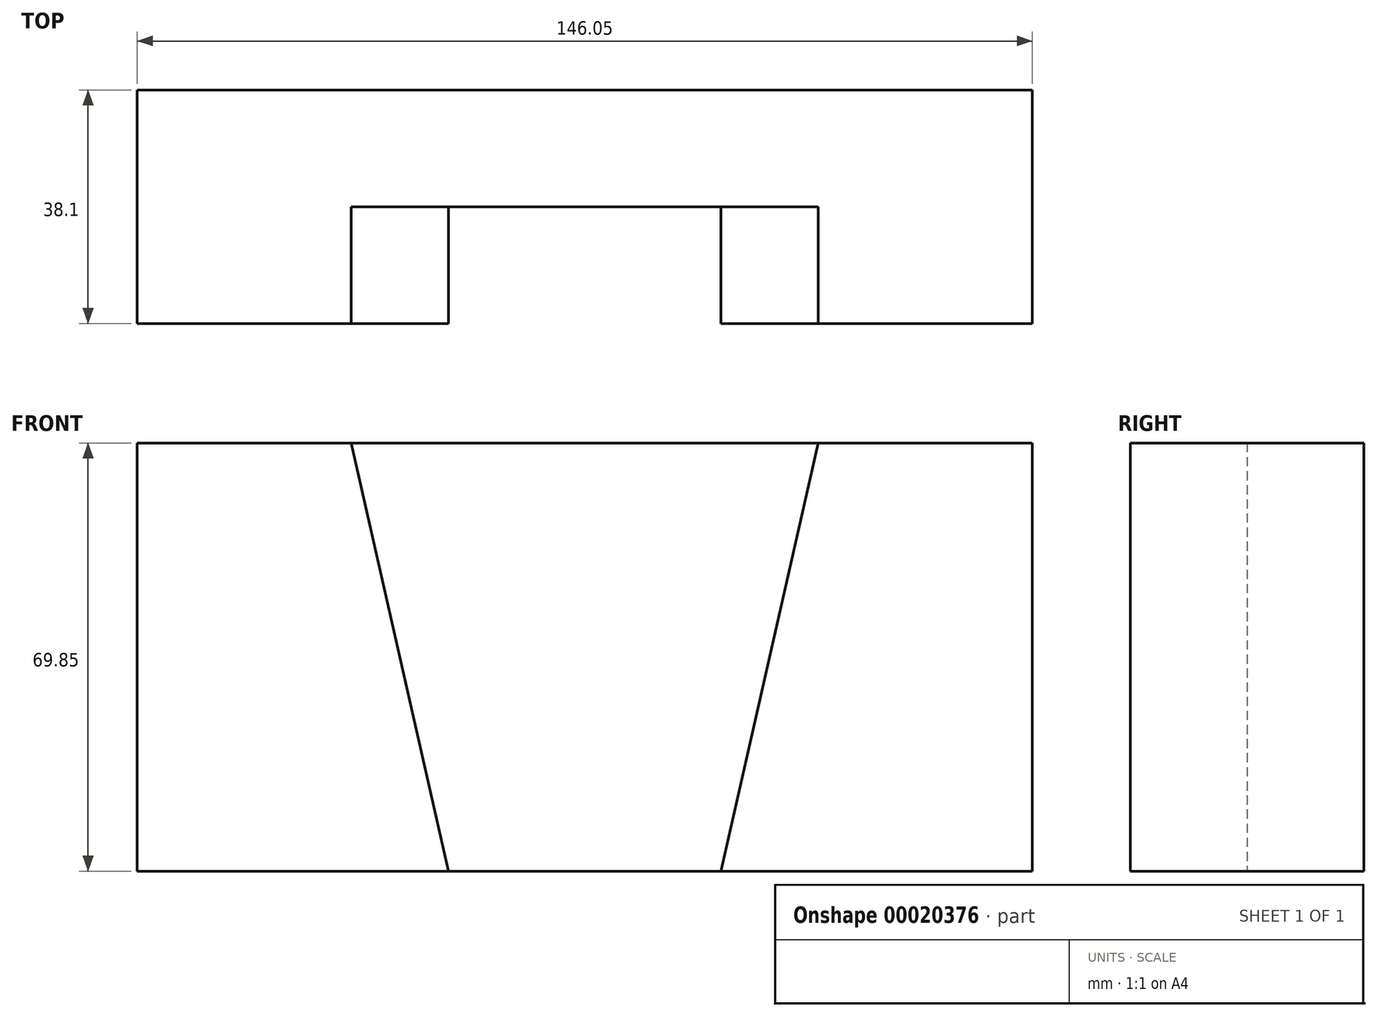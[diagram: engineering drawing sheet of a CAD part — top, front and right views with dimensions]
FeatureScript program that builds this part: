
annotation { "Feature Type Name" : "Feature", "Feature Type Description" : "" }
export const myFeature = defineFeature(function(context is Context, id is Id, definition is map)
    precondition{}
    {
        {
            var Q0;
            Q0=qCreatedBy(makeId("Front.planeOp"),FACE);
            var sketch = newSketch(context, id + "F0", { "sketchPlane" : qUnion([Q0])});
            skLineSegment(sketch, "E0.bottom", {"start": v(0, 0) * mm, "end": v(146.05, 0) * mm});
            skLineSegment(sketch, "E0.top", {"start": v(0, 69.85) * mm, "end": v(146.05, 69.85) * mm});
            skLineSegment(sketch, "E0.left", {"start": v(0, 0) * mm, "end": v(0, 69.85) * mm});
            skLineSegment(sketch, "E0.right", {"start": v(146.05, 0) * mm, "end": v(146.05, 69.85) * mm});
            skSolve(sketch);
        }
        {
            var Q0;
            Q0=makeQuery(id+"F0.imprint","IMPRINT",FACE,{"disambiguationData":[TD([[makeQuery(id+"F0.imprint","IMPRINT",EDGE,{"derivedFrom":sQuery(id+"F0.wireOp",EDGE,"E0.bottom")}),1.0]])]});
            extrude(context, id + "F1", {"entities" : qUnion([Q0]), "depth" : 19.05 * mm});
        }
        {
            var Q0;
            Q0=makeQuery(id+"F1.opExtrude","CAP_FACE",FACE,{"disambiguationData":[OSD([sQuery(id+"F0.wireOp",EDGE,"E0.bottom"),sQuery(id+"F0.wireOp",EDGE,"E0.top"),sQuery(id+"F0.wireOp",EDGE,"E0.left"),sQuery(id+"F0.wireOp",EDGE,"E0.right")])],"isStart":false});
            cPlane(context, id + "F2", {"entities" : qUnion([Q0]), "cplaneType" : CPlaneType.OFFSET, "offset" : 0 * mm, "width" : 152.4 * mm, "height" : 152.4 * mm});
        }
        {
            var Q0;
            Q0=qCreatedBy(id+"F2.planeOp",FACE);
            var sketch = newSketch(context, id + "F3", { "sketchPlane" : qUnion([Q0])});
            skLineSegment(sketch, "E1", {"start": v(0, 0) * mm, "end": v(50.8, 0) * mm});
            skLineSegment(sketch, "E2", {"start": v(50.8, 0) * mm, "end": v(95.25, 0) * mm});
            skLineSegment(sketch, "E3", {"start": v(0, 0) * mm, "end": v(0, 69.85) * mm});
            skLineSegment(sketch, "E4", {"start": v(0, 69.85) * mm, "end": v(34.93, 69.85) * mm});
            skLineSegment(sketch, "E5", {"start": v(34.93, 69.85) * mm, "end": v(50.8, 0) * mm});
            skLineSegment(sketch, "E6.MirrorCS", {"start": v(146.05, 0) * mm, "end": v(146.05, 69.85) * mm});
            skLineSegment(sketch, "E7.MirrorCS", {"start": v(146.05, 0) * mm, "end": v(95.25, 0) * mm});
            skLineSegment(sketch, "E8.MirrorCS", {"start": v(111.13, 69.85) * mm, "end": v(95.25, 0) * mm});
            skLineSegment(sketch, "E9.MirrorCS", {"start": v(146.05, 69.85) * mm, "end": v(111.12, 69.85) * mm});
            skSolve(sketch);
        }
        {
            var Q0;
            Q0=makeQuery(id+"F3.imprint","IMPRINT",FACE,{"disambiguationData":[TD([[makeQuery(id+"F3.imprint","IMPRINT",EDGE,{"derivedFrom":sQuery(id+"F3.wireOp",EDGE,"E1")}),1.0]])]});
            var Q1;
            Q1=makeQuery(id+"F3.imprint","IMPRINT",FACE,{"disambiguationData":[TD([[makeQuery(id+"F3.imprint","IMPRINT",EDGE,{"derivedFrom":sQuery(id+"F3.wireOp",EDGE,"E6.MirrorCS")}),1.0]])]});
            extrude(context, id + "F4", {"entities" : qUnion([Q0, Q1]), "operationType" : NewBodyOperationType.ADD, "depth" : 19.05 * mm});
        }
    });
